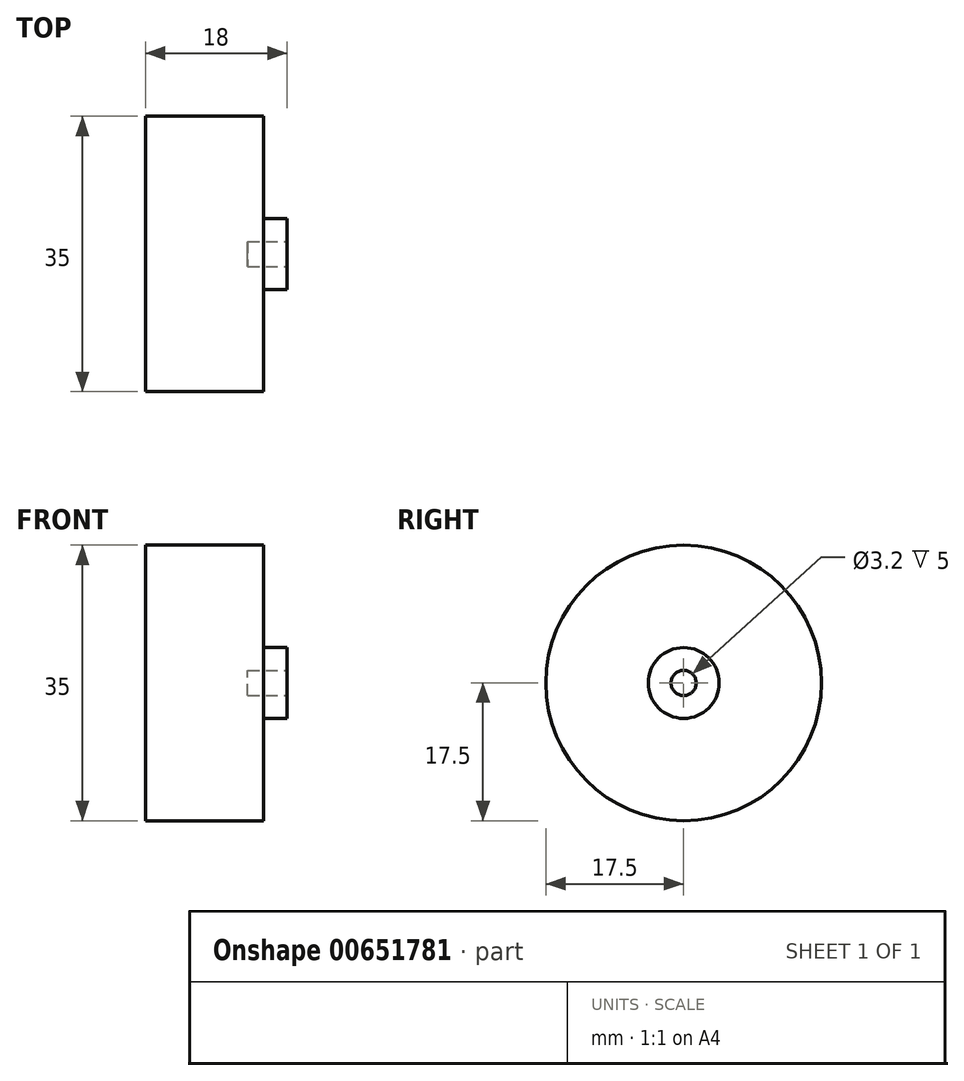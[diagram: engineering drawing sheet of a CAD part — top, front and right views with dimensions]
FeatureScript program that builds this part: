
annotation { "Feature Type Name" : "Feature", "Feature Type Description" : "" }
export const myFeature = defineFeature(function(context is Context, id is Id, definition is map)
    precondition{}
    {
        {
            var Q0;
            Q0=qCreatedBy(makeId("Right.planeOp"),FACE);
            var sketch = newSketch(context, id + "F0", { "sketchPlane" : qUnion([Q0])});
            skCircle(sketch, "E0", {"center": v(0, 0) * mm, "radius": 17.5 * mm});
            skSolve(sketch);
        }
        {
            var Q0;
            Q0=makeQuery(id+"F0.imprint","IMPRINT",FACE,{"disambiguationData":[TD([[makeQuery(id+"F0.imprint","IMPRINT",EDGE,{"derivedFrom":sQuery(id+"F0.wireOp",EDGE,"E0")}),1.0]])]});
            extrude(context, id + "F1", {"entities" : qUnion([Q0]), "depth" : 15 * mm, "offsetDistance" : 25 * mm});
        }
        {
            var Q0;
            Q0=makeQuery(id+"F1.opExtrude","CAP_FACE",FACE,{"disambiguationData":[OSD([sQuery(id+"F0.wireOp",EDGE,"E0")])],"isStart":false});
            var sketch = newSketch(context, id + "F2", { "sketchPlane" : qUnion([Q0])});
            skCircle(sketch, "E1", {"center": v(0, 0) * mm, "radius": 12.5 * mm});
            skCircle(sketch, "E2", {"center": v(0, 0) * mm, "radius": 4.5 * mm});
            skSolve(sketch);
        }
        {
            var Q0;
            Q0=makeQuery(id+"F2.imprint","IMPRINT",FACE,{"disambiguationData":[TD([[makeQuery(id+"F2.imprint","IMPRINT",EDGE,{"derivedFrom":sQuery(id+"F2.wireOp",EDGE,"E2")}),1.0]])]});
            extrude(context, id + "F3", {"entities" : qUnion([Q0]), "operationType" : NewBodyOperationType.ADD, "depth" : 3 * mm, "offsetDistance" : 25 * mm});
        }
        {
            var Q0;
            Q0=makeQuery(id+"F3.opExtrude","CAP_FACE",FACE,{"disambiguationData":[OSD([sQuery(id+"F2.wireOp",EDGE,"E2")])],"isStart":false});
            var sketch = newSketch(context, id + "F4", { "sketchPlane" : qUnion([Q0])});
            skCircle(sketch, "E3", {"center": v(0, 0) * mm, "radius": 1.6 * mm});
            skSolve(sketch);
        }
        {
            var Q0;
            Q0=makeQuery(id+"F4.imprint","IMPRINT",FACE,{"disambiguationData":[TD([[makeQuery(id+"F4.imprint","IMPRINT",EDGE,{"derivedFrom":sQuery(id+"F4.wireOp",EDGE,"E3")}),1.0]])]});
            extrude(context, id + "F5", {"entities" : qUnion([Q0]), "operationType" : NewBodyOperationType.REMOVE, "oppositeDirection" : true, "depth" : 5 * mm, "offsetDistance" : 25 * mm});
        }
    });
